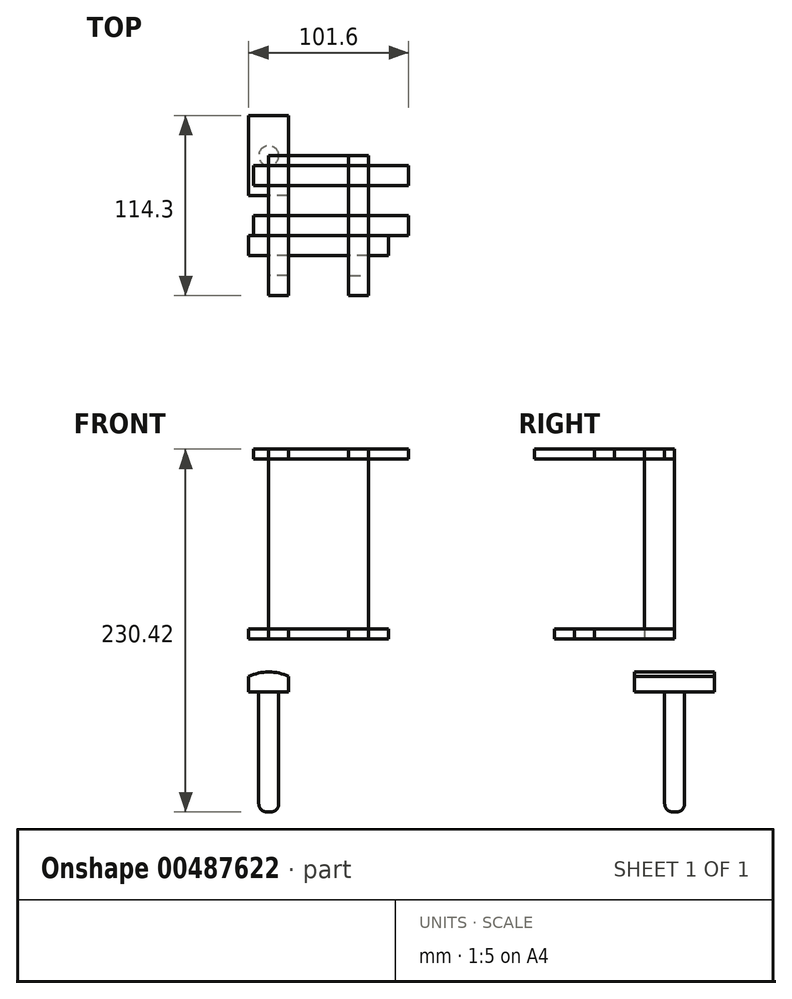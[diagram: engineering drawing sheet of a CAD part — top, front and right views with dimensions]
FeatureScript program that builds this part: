
annotation { "Feature Type Name" : "Feature", "Feature Type Description" : "" }
export const myFeature = defineFeature(function(context is Context, id is Id, definition is map)
    precondition{}
    {
        {
            var Q0;
            Q0=qCreatedBy(makeId("Front.planeOp"),FACE);
            var sketch = newSketch(context, id + "F0", { "sketchPlane" : qUnion([Q0])});
            skLineSegment(sketch, "E0.bottom", {"start": v(12.7, 0) * mm, "end": v(50.8, 0) * mm});
            skLineSegment(sketch, "E0.left", {"start": v(0, 6.35) * mm, "end": v(0, 114.3) * mm});
            skLineSegment(sketch, "E0.right", {"start": v(63.5, 6.35) * mm, "end": v(63.5, 114.3) * mm});
            skLineSegment(sketch, "E1", {"start": v(31.75, 120.65) * mm, "end": v(31.75, 0) * mm, "construction": true});
            skLineSegment(sketch, "E2", {"start": v(0, 76.2) * mm, "end": v(63.5, 76.2) * mm, "construction": true});
            skLineSegment(sketch, "E3", {"start": v(0, 6.35) * mm, "end": v(12.7, 6.35) * mm});
            skLineSegment(sketch, "E4", {"start": v(12.7, 6.35) * mm, "end": v(12.7, 0) * mm});
            skLineSegment(sketch, "E5", {"start": v(12.7, 120.65) * mm, "end": v(12.7, 114.3) * mm});
            skLineSegment(sketch, "E6", {"start": v(12.7, 114.3) * mm, "end": v(0, 114.3) * mm});
            skPoint(sketch, "E7.orphan", {"position": v(0, 0) * mm});
            skLineSegment(sketch, "E8.MirrorCS", {"start": v(12.7, 120.65) * mm, "end": v(50.8, 120.65) * mm});
            skLineSegment(sketch, "E9.MirrorCS", {"start": v(50.8, 120.65) * mm, "end": v(50.8, 114.3) * mm});
            skLineSegment(sketch, "E10.MirrorCS", {"start": v(50.8, 114.3) * mm, "end": v(63.5, 114.3) * mm});
            skLineSegment(sketch, "E11.MirrorCS", {"start": v(63.5, 6.35) * mm, "end": v(50.8, 6.35) * mm});
            skLineSegment(sketch, "E12.MirrorCS", {"start": v(50.8, 6.35) * mm, "end": v(50.8, 0) * mm});
            skPoint(sketch, "E13.orphan", {"position": v(63.5, 0) * mm});
            skSolve(sketch);
        }
        {
            var Q0;
            Q0=makeQuery(id+"F0.imprint","IMPRINT",FACE,{"disambiguationData":[TD([[makeQuery(id+"F0.imprint","IMPRINT",EDGE,{"derivedFrom":sQuery(id+"F0.wireOp",EDGE,"E0.bottom")}),1.0]])]});
            extrude(context, id + "F1", {"entities" : qUnion([Q0]), "depth" : 19.05 * mm, "offsetDistance" : 25.4 * mm});
        }
        {
            var Q0;
            Q0=qCreatedBy(makeId("Front.planeOp"),FACE);
            var sketch = newSketch(context, id + "F2", { "sketchPlane" : qUnion([Q0])});
            skLineSegment(sketch, "E14.bottom", {"start": v(12.7, 6.35) * mm, "end": v(0, 6.35) * mm});
            skLineSegment(sketch, "E14.top", {"start": v(12.7, 0) * mm, "end": v(0, 0) * mm});
            skLineSegment(sketch, "E14.left", {"start": v(12.7, 6.35) * mm, "end": v(12.7, 0) * mm});
            skLineSegment(sketch, "E14.right", {"start": v(0, 6.35) * mm, "end": v(0, 0) * mm});
            skLineSegment(sketch, "E15.bottom", {"start": v(50.8, 6.35) * mm, "end": v(63.5, 6.35) * mm});
            skLineSegment(sketch, "E15.top", {"start": v(50.8, 0) * mm, "end": v(63.5, 0) * mm});
            skLineSegment(sketch, "E15.left", {"start": v(50.8, 6.35) * mm, "end": v(50.8, 0) * mm});
            skLineSegment(sketch, "E15.right", {"start": v(63.5, 6.35) * mm, "end": v(63.5, 0) * mm});
            skSolve(sketch);
        }
        {
            var Q0;
            Q0 = qSketchRegion(id + "F2", true);
            extrude(context, id + "F3", {"entities" : qUnion([Q0]), "depth" : 76.2 * mm, "offsetDistance" : 25.4 * mm});
        }
        {
            var Q0;
            Q0=qCreatedBy(makeId("Front.planeOp"),FACE);
            var sketch = newSketch(context, id + "F4", { "sketchPlane" : qUnion([Q0])});
            skLineSegment(sketch, "E16.bottom", {"start": v(0, 120.65) * mm, "end": v(12.7, 120.65) * mm});
            skLineSegment(sketch, "E16.top", {"start": v(0, 114.3) * mm, "end": v(12.7, 114.3) * mm});
            skLineSegment(sketch, "E16.left", {"start": v(0, 120.65) * mm, "end": v(0, 114.3) * mm});
            skLineSegment(sketch, "E16.right", {"start": v(12.7, 120.65) * mm, "end": v(12.7, 114.3) * mm});
            skLineSegment(sketch, "E17.bottom", {"start": v(50.8, 120.65) * mm, "end": v(63.5, 120.65) * mm});
            skLineSegment(sketch, "E17.top", {"start": v(50.8, 114.3) * mm, "end": v(63.5, 114.3) * mm});
            skLineSegment(sketch, "E17.left", {"start": v(50.8, 120.65) * mm, "end": v(50.8, 114.3) * mm});
            skLineSegment(sketch, "E17.right", {"start": v(63.5, 120.65) * mm, "end": v(63.5, 114.3) * mm});
            skSolve(sketch);
        }
        {
            var Q0;
            Q0 = qSketchRegion(id + "F4", true);
            extrude(context, id + "F5", {"entities" : qUnion([Q0]), "depth" : 88.9 * mm, "offsetDistance" : 25.4 * mm});
        }
        {
            var Q0;
            Q0=qCreatedBy(makeId("Front.planeOp"),FACE);
            var sketch = newSketch(context, id + "F6", { "sketchPlane" : qUnion([Q0])});
            skArc(sketch, "E18", {"start": v(12.7, -23.86) * mm, "mid": v(0, -20.87) * mm, "end": v(-12.7, -23.86) * mm});
            skLineSegment(sketch, "E19", {"start": v(12.7, -23.86) * mm, "end": v(12.7, -33.57) * mm});
            skLineSegment(sketch, "E20", {"start": v(12.7, -33.57) * mm, "end": v(-12.7, -33.57) * mm});
            skLineSegment(sketch, "E21", {"start": v(-12.7, -33.57) * mm, "end": v(-12.7, -23.86) * mm});
            skLineSegment(sketch, "E22", {"start": v(0, 0) * mm, "end": v(0, -33.57) * mm, "construction": true});
            skSolve(sketch);
        }
        {
            var Q0;
            Q0=makeQuery(id+"F6.imprint","IMPRINT",FACE,{"disambiguationData":[TD([[makeQuery(id+"F6.imprint","IMPRINT",EDGE,{"derivedFrom":sQuery(id+"F6.wireOp",EDGE,"E18")}),1.0]])]});
            extrude(context, id + "F7", {"entities" : qUnion([Q0]), "endBound" : BoundingType.SYMMETRIC, "depth" : 50.8 * mm});
        }
        {
            var Q0;
            Q0=makeQuery(id+"F7.opExtrude","SWEPT_FACE",FACE,{"disambiguationData":[OSD([sQuery(id+"F6.wireOp",EDGE,"E20")])]});
            var sketch = newSketch(context, id + "F8", { "sketchPlane" : qUnion([Q0])});
            skCircle(sketch, "E23", {"center": v(0, 0) * mm, "radius": 6.35 * mm});
            skSolve(sketch);
        }
        {
            var Q0;
            Q0=makeQuery(id+"F8.imprint","IMPRINT",FACE,{"disambiguationData":[TD([[makeQuery(id+"F8.imprint","IMPRINT",EDGE,{"derivedFrom":sQuery(id+"F8.wireOp",EDGE,"E23")}),1.0]])]});
            extrude(context, id + "F9", {"entities" : qUnion([Q0]), "operationType" : NewBodyOperationType.ADD, "depth" : 76.2 * mm});
        }
        {
            var Q0;
            Q0=makeQuery(id+"F9.opExtrude","CAP_EDGE",EDGE,{"disambiguationData":[OSD([sQuery(id+"F8.wireOp",EDGE,"E23")])],"isStart":false});
            fillet(context, id + "F10", {"entities" : qUnion([Q0]), "radius" : 5.08 * mm, "tangentPropagation" : true, "allowEdgeOverflow" : false});
        }
        {
            var Q0;
            Q0=makeQuery(id+"F5.opExtrude","SWEPT_FACE",FACE,{"disambiguationData":[OSD([sQuery(id+"F4.wireOp",EDGE,"E16.bottom")])]});
            var sketch = newSketch(context, id + "F11", { "sketchPlane" : qUnion([Q0])});
            skLineSegment(sketch, "E24.top", {"start": v(-9.53, -6.35) * mm, "end": v(88.9, -6.35) * mm});
            skLineSegment(sketch, "E24.right", {"start": v(88.9, -19.05) * mm, "end": v(88.9, -6.35) * mm});
            skLineSegment(sketch, "E25.bottom", {"start": v(-9.53, -38.1) * mm, "end": v(88.9, -38.1) * mm});
            skLineSegment(sketch, "E25.top", {"start": v(-9.53, -50.8) * mm, "end": v(88.9, -50.8) * mm});
            skLineSegment(sketch, "E25.left", {"start": v(-9.53, -38.1) * mm, "end": v(-9.53, -50.8) * mm});
            skLineSegment(sketch, "E25.right", {"start": v(88.9, -38.1) * mm, "end": v(88.9, -50.8) * mm});
            skLineSegment(sketch, "E26", {"start": v(88.9, -19.05) * mm, "end": v(-9.53, -19.05) * mm});
            skLineSegment(sketch, "E27", {"start": v(-9.53, -19.05) * mm, "end": v(-9.53, -6.35) * mm});
            skSolve(sketch);
        }
        {
            var Q0;
            Q0 = qSketchRegion(id + "F11", true);
            var Q1;
            Q1=makeQuery(id+"F5.opExtrude","SWEPT_FACE",FACE,{"disambiguationData":[OSD([sQuery(id+"F4.wireOp",EDGE,"E16.top")])]});
            extrude(context, id + "F12", {"entities" : qUnion([Q0]), "endBound" : BoundingType.UP_TO_SURFACE, "oppositeDirection" : true, "depth" : 12.7 * mm, "endBoundEntityFace" : qUnion([Q1]), "offsetDistance" : 25.4 * mm});
        }
        {
            var Q0;
            Q0=qCreatedBy(makeId("Top.planeOp"),FACE);
            var sketch = newSketch(context, id + "F13", { "sketchPlane" : qUnion([Q0])});
            skLineSegment(sketch, "E28.bottom", {"start": v(-12.7, -63.5) * mm, "end": v(76.2, -63.5) * mm});
            skLineSegment(sketch, "E28.top", {"start": v(-12.7, -50.8) * mm, "end": v(76.2, -50.8) * mm});
            skLineSegment(sketch, "E28.left", {"start": v(-12.7, -63.5) * mm, "end": v(-12.7, -50.8) * mm});
            skLineSegment(sketch, "E28.right", {"start": v(76.2, -63.5) * mm, "end": v(76.2, -50.8) * mm});
            skLineSegment(sketch, "E29", {"start": v(0, -76.2) * mm, "end": v(0, -63.5) * mm, "construction": true});
            skLineSegment(sketch, "E30", {"start": v(0, -63.5) * mm, "end": v(-12.7, -63.5) * mm, "construction": true});
            skLineSegment(sketch, "E31", {"start": v(76.2, -63.5) * mm, "end": v(63.5, -76.2) * mm, "construction": true});
            skSolve(sketch);
        }
        {
            var Q0;
            Q0=makeQuery(id+"F13.imprint","IMPRINT",FACE,{"disambiguationData":[TD([[makeQuery(id+"F13.imprint","IMPRINT",EDGE,{"derivedFrom":sQuery(id+"F13.wireOp",EDGE,"E28.bottom")}),1.0]])]});
            var Q1;
            Q1=makeQuery(id+"F3.opExtrude","SWEPT_FACE",FACE,{"disambiguationData":[OSD([sQuery(id+"F2.wireOp",EDGE,"E14.bottom")])]});
            extrude(context, id + "F14", {"entities" : qUnion([Q0]), "endBound" : BoundingType.UP_TO_SURFACE, "depth" : 25.4 * mm, "endBoundEntityFace" : qUnion([Q1]), "offsetDistance" : 25.4 * mm});
        }
        {
            var Q0;
            Q0=makeQuery(id+"F12.opExtrude","SWEPT_BODY",BODY,{"disambiguationData":[OSD([sQuery(id+"F11.wireOp",EDGE,"E24.top"),sQuery(id+"F11.wireOp",EDGE,"E24.right"),sQuery(id+"F11.wireOp",EDGE,"E26"),sQuery(id+"F11.wireOp",EDGE,"E27")])]});
            var Q1;
            Q1=makeQuery(id+"F1.opExtrude","SWEPT_BODY",BODY,{"disambiguationData":[OSD([sQuery(id+"F0.wireOp",EDGE,"E0.bottom"),sQuery(id+"F0.wireOp",EDGE,"E0.left"),sQuery(id+"F0.wireOp",EDGE,"E0.right"),sQuery(id+"F0.wireOp",EDGE,"E3"),sQuery(id+"F0.wireOp",EDGE,"E4"),sQuery(id+"F0.wireOp",EDGE,"E5"),sQuery(id+"F0.wireOp",EDGE,"E6"),sQuery(id+"F0.wireOp",EDGE,"E8.MirrorCS"),sQuery(id+"F0.wireOp",EDGE,"E9.MirrorCS"),sQuery(id+"F0.wireOp",EDGE,"E10.MirrorCS"),sQuery(id+"F0.wireOp",EDGE,"E11.MirrorCS"),sQuery(id+"F0.wireOp",EDGE,"E12.MirrorCS")])]});
            booleanBodies(context, id + "F15", {"operationType" : BooleanOperationType.SUBTRACTION, "tools" : qUnion([Q0]), "targets" : qUnion([Q1]), "keepTools" : true});
        }
    });
